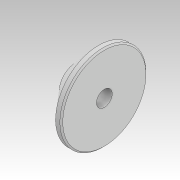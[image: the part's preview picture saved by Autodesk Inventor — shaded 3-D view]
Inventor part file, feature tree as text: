
AUTODESK INVENTOR PART (.ipt)
format: ipt  version: 2020 (Build 240168000, 168)  size: 98,816 bytes
history: native  units: mm
features: revolve x1, sketch x1
ambient origin geometry x8: Origin, YZ Plane, XZ Plane, XY Plane, X Axis, Y Axis, Z Axis, Center Point
bodies: Solid1 (feature_tree)
feature tree (2):
  revolve  "Revolution1"  [1 undecoded]
  sketch  "Sketch1"  dims[d0=2.75mm d1=10.0mm d2=3.0mm d3=2.0mm d4=15.0mm d5=0.5mm d6=0.5mm d7=90.0deg]
note: 1 required parameter value undecoded (feature->parameter linkage not recoverable at this tier; creation-order binding heuristic only, values carry confidence <= 0.55)
